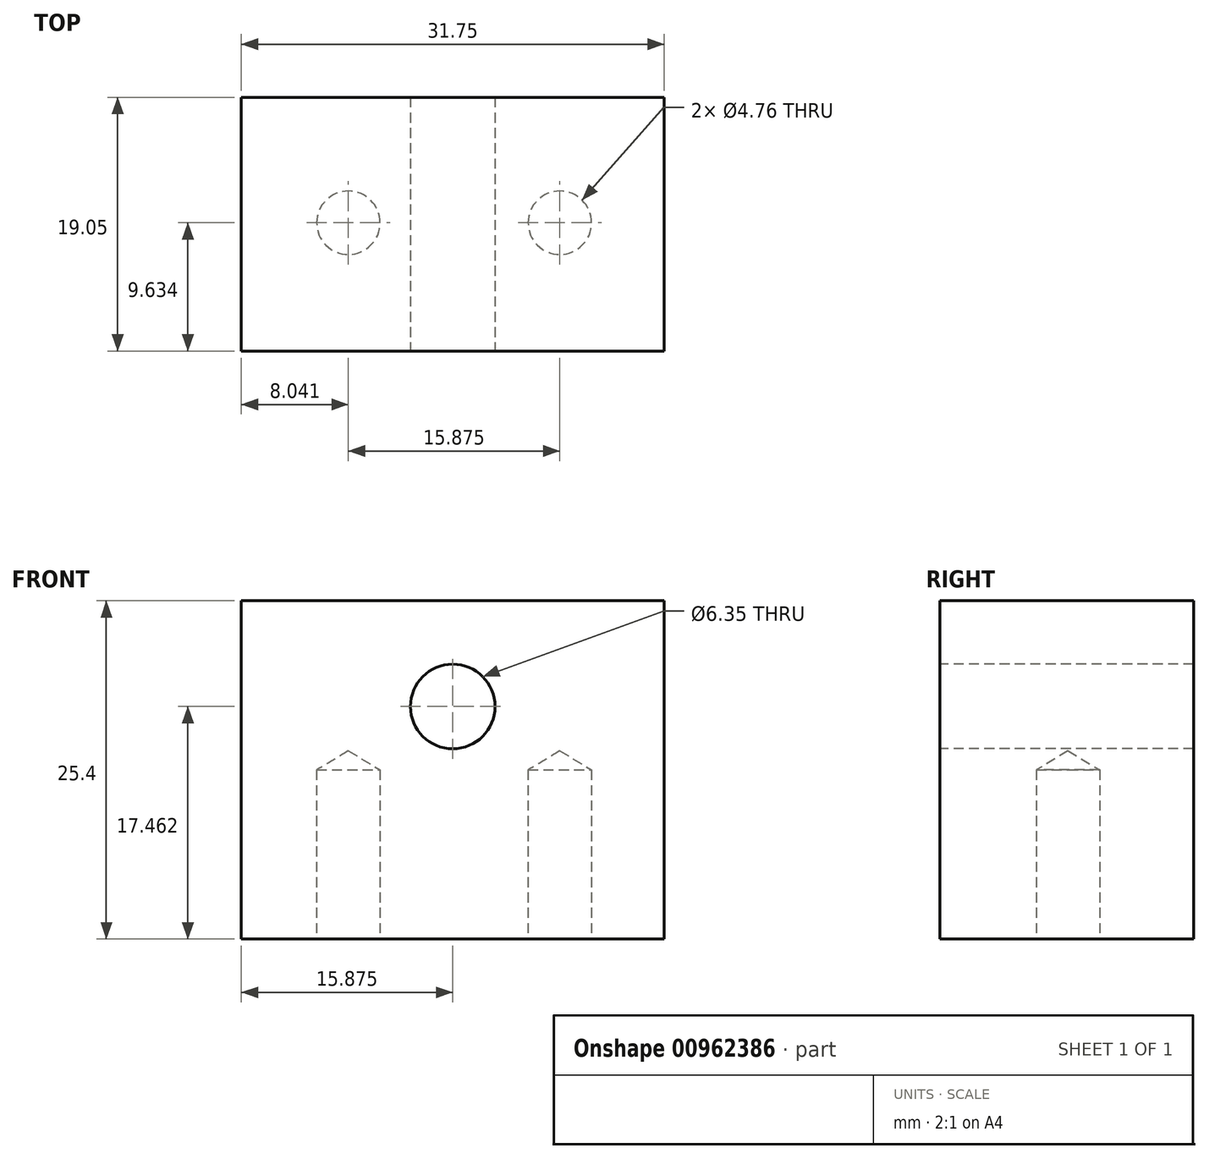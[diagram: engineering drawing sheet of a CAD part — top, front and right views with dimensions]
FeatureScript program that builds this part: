
annotation { "Feature Type Name" : "Feature", "Feature Type Description" : "" }
export const myFeature = defineFeature(function(context is Context, id is Id, definition is map)
    precondition{}
    {
        {
            var Q0;
            Q0=qCreatedBy(makeId("Top.planeOp"),FACE);
            var sketch = newSketch(context, id + "F0", { "sketchPlane" : qUnion([Q0])});
            skLineSegment(sketch, "E0.bottom", {"start": v(0, 0) * mm, "end": v(31.75, 0) * mm});
            skLineSegment(sketch, "E0.top", {"start": v(0, 19.05) * mm, "end": v(31.75, 19.05) * mm});
            skLineSegment(sketch, "E0.left", {"start": v(0, 0) * mm, "end": v(0, 19.05) * mm});
            skLineSegment(sketch, "E0.right", {"start": v(31.75, 0) * mm, "end": v(31.75, 19.05) * mm});
            skSolve(sketch);
        }
        {
            var Q0;
            Q0 = qSketchRegion(id + "F0", true);
            extrude(context, id + "F1", {"entities" : qUnion([Q0]), "depth" : 25.4 * mm, "offsetDistance" : 25.4 * mm});
        }
        {
            var Q0;
            Q0=makeQuery(id+"F0.imprint","IMPRINT",FACE,{"disambiguationData":[TD([[makeQuery(id+"F0.imprint","IMPRINT",EDGE,{"derivedFrom":sQuery(id+"F0.wireOp",EDGE,"E0.bottom")}),1.0]])]});
            var sketch = newSketch(context, id + "F2", { "sketchPlane" : qUnion([Q0])});
            skLineSegment(sketch, "E1.bottom", {"start": v(0.1, 0.1) * mm, "end": v(31.85, 0.1) * mm});
            skLineSegment(sketch, "E1.top", {"start": v(0.1, 19.16) * mm, "end": v(31.85, 19.16) * mm});
            skLineSegment(sketch, "E1.left", {"start": v(0.1, 0.1) * mm, "end": v(0.1, 19.16) * mm});
            skLineSegment(sketch, "E1.right", {"start": v(31.85, 0.1) * mm, "end": v(31.85, 19.16) * mm});
            skCircle(sketch, "E2", {"center": v(8.04, 9.63) * mm, "radius": 2.38 * mm});
            skCircle(sketch, "E3", {"center": v(23.92, 9.63) * mm, "radius": 2.38 * mm});
            skSolve(sketch);
        }
        {
            var Q0;
            Q0=sQuery(id+"F2.wireOp",VERTEX,"E2.center");
            var Q1;
            Q1=sQuery(id+"F2.wireOp",VERTEX,"E3.center");
            var Q2;
            Q2=makeQuery(id+"F1.opExtrude","SWEPT_BODY",BODY,{"disambiguationData":[OSD([sQuery(id+"F0.wireOp",EDGE,"E0.bottom"),sQuery(id+"F0.wireOp",EDGE,"E0.top"),sQuery(id+"F0.wireOp",EDGE,"E0.left"),sQuery(id+"F0.wireOp",EDGE,"E0.right")])]});
            hole(context, id + "F3", {"style" : HoleStyle.SIMPLE, "endStyle" : HoleEndStyle.BLIND, "oppositeDirection" : true, "holeDiameter" : 4.76 * mm, "majorDiameter" : 6.35 * mm, "holeDepth" : 12.7 * mm, "isTappedThrough" : true, "tappedDepth" : 12.7 * mm, "tapClearance" : 3, "startFromSketch" : true, "locations" : qUnion([Q0, Q1]), "scope" : qUnion([Q2])});
        }
        {
            var Q0;
            Q0=makeQuery(id+"F1.opExtrude","SWEPT_FACE",FACE,{"disambiguationData":[OSD([sQuery(id+"F0.wireOp",EDGE,"E0.bottom")])]});
            var sketch = newSketch(context, id + "F4", { "sketchPlane" : qUnion([Q0])});
            skCircle(sketch, "E4", {"center": v(15.88, 17.46) * mm, "radius": 3.18 * mm});
            skSolve(sketch);
        }
        {
            var Q0;
            Q0=sQuery(id+"F4.wireOp",VERTEX,"E4.center");
            var Q1;
            Q1=makeQuery(id+"F1.opExtrude","SWEPT_BODY",BODY,{"disambiguationData":[OSD([sQuery(id+"F0.wireOp",EDGE,"E0.bottom"),sQuery(id+"F0.wireOp",EDGE,"E0.top"),sQuery(id+"F0.wireOp",EDGE,"E0.left"),sQuery(id+"F0.wireOp",EDGE,"E0.right")])]});
            hole(context, id + "F5", {"style" : HoleStyle.SIMPLE, "endStyle" : HoleEndStyle.THROUGH, "holeDiameter" : 6.35 * mm, "majorDiameter" : 6.35 * mm, "isTappedThrough" : true, "tappedDepth" : 12.7 * mm, "tapClearance" : 3, "startFromSketch" : true, "locations" : qUnion([Q0]), "scope" : qUnion([Q1])});
        }
    });
